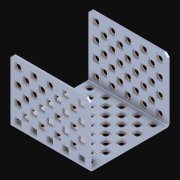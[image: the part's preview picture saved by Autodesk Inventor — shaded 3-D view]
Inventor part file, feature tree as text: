
AUTODESK INVENTOR PART (.ipt)
format: ipt  version: 2021 (Build 250183000, 183)  size: 831,488 bytes
history: native  units: in
note: dims shown in document units (in); Inventor stores cm internally (conversion verified against a paired STEP export)
features: other x106, extrude x105, pattern_linear x6, sketch x3, imported_body x1
ambient origin geometry x8: Origin, YZ Plane, XZ Plane, XY Plane, X Axis, Y Axis, Z Axis, Center Point
bodies: Body1 (feature_tree), Body2 (feature_tree), Body3 (feature_tree), Body4 (feature_tree), Body5 (feature_tree), Body6 (feature_tree), Body7 (feature_tree), Body8 (feature_tree), Body9 (feature_tree), Body10 (feature_tree), Body11 (feature_tree), Body12 (feature_tree), Body13 (feature_tree), Body14 (feature_tree), Body15 (feature_tree), Body16 (feature_tree), Body17 (feature_tree), Body18 (feature_tree), Body19 (feature_tree), Body20 (feature_tree), Body21 (feature_tree), Body22 (feature_tree), Body23 (feature_tree), Body24 (feature_tree), Body25 (feature_tree), Body26 (feature_tree), Body27 (feature_tree), Body28 (feature_tree), Body29 (feature_tree), Body30 (feature_tree), Body31 (feature_tree), Body32 (feature_tree), Body33 (feature_tree), Body34 (feature_tree), Body35 (feature_tree), Body36 (feature_tree), Body37 (feature_tree), Body38 (feature_tree), Body39 (feature_tree), Body40 (feature_tree), Body41 (feature_tree), Body42 (feature_tree), Body43 (feature_tree), Body44 (feature_tree), Body45 (feature_tree), Body46 (feature_tree), Body47 (feature_tree), Body48 (feature_tree), Body49 (feature_tree), Body50 (feature_tree), Body51 (feature_tree), Body52 (feature_tree), Body53 (feature_tree), Body54 (feature_tree), Body55 (feature_tree), Body56 (feature_tree), Body57 (feature_tree), Body58 (feature_tree), Body59 (feature_tree), Body60 (feature_tree), Body61 (feature_tree), Body62 (feature_tree), Body63 (feature_tree), Body64 (feature_tree), Body65 (feature_tree), Body66 (feature_tree), Body67 (feature_tree), Body68 (feature_tree), Body69 (feature_tree), Body70 (feature_tree), Body71 (feature_tree), Body72 (feature_tree), Body73 (feature_tree), Body74 (feature_tree), Body75 (feature_tree), Body76 (feature_tree), Body77 (feature_tree), Body78 (feature_tree), Body79 (feature_tree), Body80 (feature_tree), Body81 (feature_tree), Body82 (feature_tree), Body83 (feature_tree), Body84 (feature_tree), Body85 (feature_tree), Body86 (feature_tree), Body87 (feature_tree), Body88 (feature_tree), Body89 (feature_tree), Body90 (feature_tree), Body91 (feature_tree), Body92 (feature_tree), Body93 (feature_tree), Body94 (feature_tree), Body95 (feature_tree), Body96 (feature_tree), Body97 (feature_tree), Body98 (feature_tree), Body99 (feature_tree), Body100 (feature_tree), Body101 (feature_tree), Body102 (feature_tree), Body103 (feature_tree), Body104 (feature_tree), Body105 (feature_tree), Body106 (feature_tree)
feature tree (221):
  other  "LPattern4"
  imported_body  "Base1"
  pattern_linear  "Rectangular Pattern1"  Count1=4 Spacing1=0.5in
  pattern_linear  "Rectangular Pattern2"  Count1=5 Spacing1=0.5in
  pattern_linear  "Rectangular Pattern3"  Count1=3 Spacing1=0.5in
  pattern_linear  "Rectangular Pattern4"  Count1=4 Spacing1=0.5in
  pattern_linear  "Rectangular Pattern5"  Count1=4 Spacing1=0.5in
  pattern_linear  "Rectangular Pattern6"  Count1=5 Spacing1=0.5in
  other  "Srf1"
  other  "Srf2"
  other  "Srf3"
  other  "Srf4"
  other  "Srf5"
  other  "Srf6"
  other  "Srf7"
  other  "Srf8"
  other  "Srf9"
  other  "Srf10"
  other  "Srf11"
  other  "Srf12"
  other  "Srf13"
  other  "Srf14"
  other  "Srf15"
  other  "Srf16"
  other  "Srf17"
  other  "Srf18"
  other  "Srf19"
  other  "Srf20"
  other  "Srf21"
  other  "Srf22"
  other  "Srf23"
  other  "Srf24"
  other  "Srf25"
  other  "Srf26"
  other  "Srf27"
  other  "Srf28"
  other  "Srf29"
  other  "Srf30"
  other  "Srf31"
  other  "Srf32"
  other  "Srf33"
  other  "Srf34"
  other  "Srf35"
  other  "Srf36"
  other  "Srf37"
  other  "Srf38"
  other  "Srf39"
  other  "Srf40"
  other  "Srf41"
  other  "Srf42"
  other  "Srf43"
  other  "Srf44"
  other  "Srf45"
  other  "Srf46"
  other  "Srf47"
  other  "Srf48"
  other  "Srf49"
  other  "Srf50"
  other  "Srf51"
  other  "Srf52"
  sketch  "Sketch4"  dims[d49=0.046in d50=0.0in d51=1.5748in d53=0.5in d54=1.9685in d56=0.5in]
  other  "Srf53"
  other  "Srf54"
  other  "Srf55"
  other  "Srf56"
  other  "Srf57"
  other  "Srf58"
  other  "Srf59"
  other  "Srf60"
  other  "Srf61"
  other  "Srf62"
  other  "Srf63"
  other  "Srf64"
  sketch  "Sketch5"  dims[d58=0.046in d59=0.0in d60=1.1811in d62=0.5in d63=1.5748in d65=0.5in]
  other  "Srf65"
  other  "Srf66"
  other  "Srf67"
  other  "Srf68"
  other  "Srf69"
  other  "Srf70"
  other  "Srf71"
  other  "Srf72"
  other  "Srf73"
  other  "Srf74"
  other  "Srf75"
  other  "Srf76"
  other  "Srf77"
  other  "Srf78"
  other  "Srf79"
  other  "Srf80"
  other  "Srf81"
  other  "Srf82"
  other  "Srf83"
  other  "Srf84"
  other  "Srf85"
  other  "Srf86"
  other  "Srf87"
  other  "Srf88"
  other  "Srf89"
  sketch  "Sketch6"  dims[d67=0.046in d68=0.0in d69=1.5748in d71=0.5in d72=1.9685in d74=0.5in d76=0.046in d77=0.0in d78=1.1811in d80=0.5in d81=1.5748in d83=0.5in d85=0.046in d86=0.0in d87=1.9685in d89=0.5in d90=1.9685in d92=0.5in d94=0.046in d95=0.0in d96=1.5748in d98=0.5in d99=1.5748in d101=0.5in]
  other  "Srf90"
  other  "Srf91"
  other  "Srf92"
  other  "Srf93"
  other  "Srf94"
  other  "Srf95"
  other  "Srf96"
  other  "Srf97"
  other  "Srf98"
  other  "Srf99"
  other  "Srf100"
  other  "Srf101"
  other  "Srf102"
  other  "Srf103"
  other  "Srf104"
  other  "Srf105"
  extrude  "ExtrusionSrf1"  Depth=0.5in TaperAngle=0.0deg
  extrude  "ExtrusionSrf21"  Depth=0.5in
  extrude  "ExtrusionSrf33"  Depth=0.5in
  extrude  "ExtrusionSrf53"  Depth=0.5in TaperAngle=0.0deg
  extrude  "ExtrusionSrf65"  Depth=0.5in
  extrude  "ExtrusionSrf90"  Depth=0.5in
  extrude  "ExtrusionSrf2"  Depth=0.5in TaperAngle=0.0deg
  extrude  "ExtrusionSrf3"  Depth=0.5in
  extrude  "ExtrusionSrf4"  Depth=0.5in
  extrude  "ExtrusionSrf5"  [1 undecoded]
  extrude  "ExtrusionSrf6"  [1 undecoded]
  extrude  "ExtrusionSrf7"  [1 undecoded]
  extrude  "ExtrusionSrf8"  [1 undecoded]
  extrude  "ExtrusionSrf9"  [1 undecoded]
  extrude  "ExtrusionSrf10"  [1 undecoded]
  extrude  "ExtrusionSrf11"  [1 undecoded]
  extrude  "ExtrusionSrf12"  [1 undecoded]
  extrude  "ExtrusionSrf13"  [1 undecoded]
  extrude  "ExtrusionSrf14"  [1 undecoded]
  extrude  "ExtrusionSrf15"  [1 undecoded]
  extrude  "ExtrusionSrf16"  [1 undecoded]
  extrude  "ExtrusionSrf17"  [1 undecoded]
  extrude  "ExtrusionSrf18"  [1 undecoded]
  extrude  "ExtrusionSrf19"  [1 undecoded]
  extrude  "ExtrusionSrf20"  [1 undecoded]
  extrude  "ExtrusionSrf22"  [1 undecoded]
  extrude  "ExtrusionSrf23"  [1 undecoded]
  extrude  "ExtrusionSrf24"  [1 undecoded]
  extrude  "ExtrusionSrf25"  [1 undecoded]
  extrude  "ExtrusionSrf26"  [1 undecoded]
  extrude  "ExtrusionSrf27"  [1 undecoded]
  extrude  "ExtrusionSrf28"  [1 undecoded]
  extrude  "ExtrusionSrf29"  [1 undecoded]
  extrude  "ExtrusionSrf30"  [1 undecoded]
  extrude  "ExtrusionSrf31"  [1 undecoded]
  extrude  "ExtrusionSrf32"  [1 undecoded]
  extrude  "ExtrusionSrf34"  [1 undecoded]
  extrude  "ExtrusionSrf35"  [1 undecoded]
  extrude  "ExtrusionSrf36"  [1 undecoded]
  extrude  "ExtrusionSrf37"  [1 undecoded]
  extrude  "ExtrusionSrf38"  [1 undecoded]
  extrude  "ExtrusionSrf39"  [1 undecoded]
  extrude  "ExtrusionSrf40"  [1 undecoded]
  extrude  "ExtrusionSrf41"  [1 undecoded]
  extrude  "ExtrusionSrf42"  [1 undecoded]
  extrude  "ExtrusionSrf43"  [1 undecoded]
  extrude  "ExtrusionSrf44"  [1 undecoded]
  extrude  "ExtrusionSrf45"  [1 undecoded]
  extrude  "ExtrusionSrf46"  [1 undecoded]
  extrude  "ExtrusionSrf47"  [1 undecoded]
  extrude  "ExtrusionSrf48"  [1 undecoded]
  extrude  "ExtrusionSrf49"  [1 undecoded]
  extrude  "ExtrusionSrf50"  [1 undecoded]
  extrude  "ExtrusionSrf51"  [1 undecoded]
  extrude  "ExtrusionSrf52"  [1 undecoded]
  extrude  "ExtrusionSrf54"  [1 undecoded]
  extrude  "ExtrusionSrf55"  [1 undecoded]
  extrude  "ExtrusionSrf56"  [1 undecoded]
  extrude  "ExtrusionSrf57"  [1 undecoded]
  extrude  "ExtrusionSrf58"  [1 undecoded]
  extrude  "ExtrusionSrf59"  [1 undecoded]
  extrude  "ExtrusionSrf60"  [1 undecoded]
  extrude  "ExtrusionSrf61"  [1 undecoded]
  extrude  "ExtrusionSrf62"  [1 undecoded]
  extrude  "ExtrusionSrf63"  [1 undecoded]
  extrude  "ExtrusionSrf64"  [1 undecoded]
  extrude  "ExtrusionSrf66"  [1 undecoded]
  extrude  "ExtrusionSrf67"  [1 undecoded]
  extrude  "ExtrusionSrf68"  [1 undecoded]
  extrude  "ExtrusionSrf69"  [1 undecoded]
  extrude  "ExtrusionSrf70"  [1 undecoded]
  extrude  "ExtrusionSrf71"  [1 undecoded]
  extrude  "ExtrusionSrf72"  [1 undecoded]
  extrude  "ExtrusionSrf73"  [1 undecoded]
  extrude  "ExtrusionSrf74"  [1 undecoded]
  extrude  "ExtrusionSrf75"  [1 undecoded]
  extrude  "ExtrusionSrf76"  [1 undecoded]
  extrude  "ExtrusionSrf77"  [1 undecoded]
  extrude  "ExtrusionSrf78"  [1 undecoded]
  extrude  "ExtrusionSrf79"  [1 undecoded]
  extrude  "ExtrusionSrf80"  [1 undecoded]
  extrude  "ExtrusionSrf81"  [1 undecoded]
  extrude  "ExtrusionSrf82"  [1 undecoded]
  extrude  "ExtrusionSrf83"  [1 undecoded]
  extrude  "ExtrusionSrf84"  [1 undecoded]
  extrude  "ExtrusionSrf85"  [1 undecoded]
  extrude  "ExtrusionSrf86"  [1 undecoded]
  extrude  "ExtrusionSrf87"  [1 undecoded]
  extrude  "ExtrusionSrf88"  [1 undecoded]
  extrude  "ExtrusionSrf89"  [1 undecoded]
  extrude  "ExtrusionSrf91"  [1 undecoded]
  extrude  "ExtrusionSrf92"  [1 undecoded]
  extrude  "ExtrusionSrf93"  [1 undecoded]
  extrude  "ExtrusionSrf94"  [1 undecoded]
  extrude  "ExtrusionSrf95"  [1 undecoded]
  extrude  "ExtrusionSrf96"  [1 undecoded]
  extrude  "ExtrusionSrf97"  [1 undecoded]
  extrude  "ExtrusionSrf98"  [1 undecoded]
  extrude  "ExtrusionSrf99"  [1 undecoded]
  extrude  "ExtrusionSrf100"  [1 undecoded]
  extrude  "ExtrusionSrf101"  [1 undecoded]
  extrude  "ExtrusionSrf102"  [1 undecoded]
  extrude  "ExtrusionSrf103"  [1 undecoded]
  extrude  "ExtrusionSrf104"  [1 undecoded]
  extrude  "ExtrusionSrf105"  [1 undecoded]
note: 96 required parameter values undecoded (feature->parameter linkage not recoverable at this tier; creation-order binding heuristic only, values carry confidence <= 0.55)
